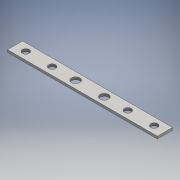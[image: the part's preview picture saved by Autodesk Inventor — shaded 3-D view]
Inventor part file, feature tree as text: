
AUTODESK INVENTOR PART (.ipt)
format: ipt  version: 2016 (Build 200138000, 138)  size: 110,080 bytes
history: native  units: mm
features: extrude x1, sketch x1
ambient origin geometry x8: Origin, YZ Plane, XZ Plane, XY Plane, X Axis, Y Axis, Z Axis, Center Point
bodies: Solid1 (feature_tree)
feature tree (2):
  extrude  "Extrusion1"  Depth=9.525mm
  sketch  "Sketch1"  dims[d4=26.0mm d6=26.0mm d8=32.0mm d10=26.0mm d12=26.0mm d14=32.0mm d16=568.96mm d17=57.15mm d18=40.64mm d19=140.776mm d20=230.152mm d21=230.152mm d22=40.64mm d23=140.776mm d24=9.525mm d25=0.0mm]
